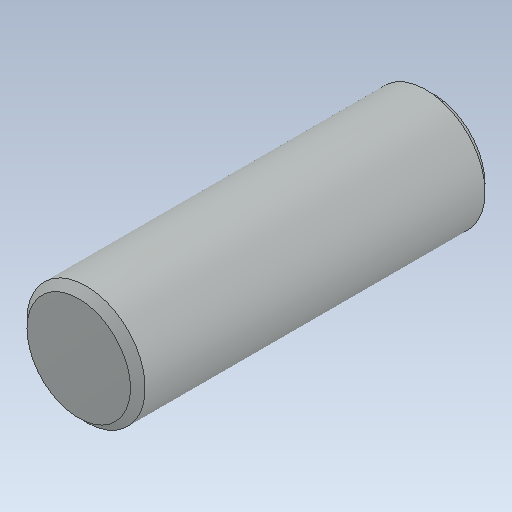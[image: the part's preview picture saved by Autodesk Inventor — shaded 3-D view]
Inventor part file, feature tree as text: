
AUTODESK INVENTOR PART (.ipt)
format: ipt  version: 2020 (Build 240168000, 168)  size: 102,912 bytes
history: native  units: in
note: dims shown in document units (in); Inventor stores cm internally (conversion verified against a paired STEP export)
features: chamfer x1
ambient origin geometry x8: Origin, YZ Plane, XZ Plane, XY Plane, X Axis, Y Axis, Z Axis, Center Point
bodies: Solid1 (feature_tree)
feature tree (1):
  chamfer  "Chamfer1"  [1 undecoded]
note: 1 required parameter value undecoded (feature->parameter linkage not recoverable at this tier; creation-order binding heuristic only, values carry confidence <= 0.55)
